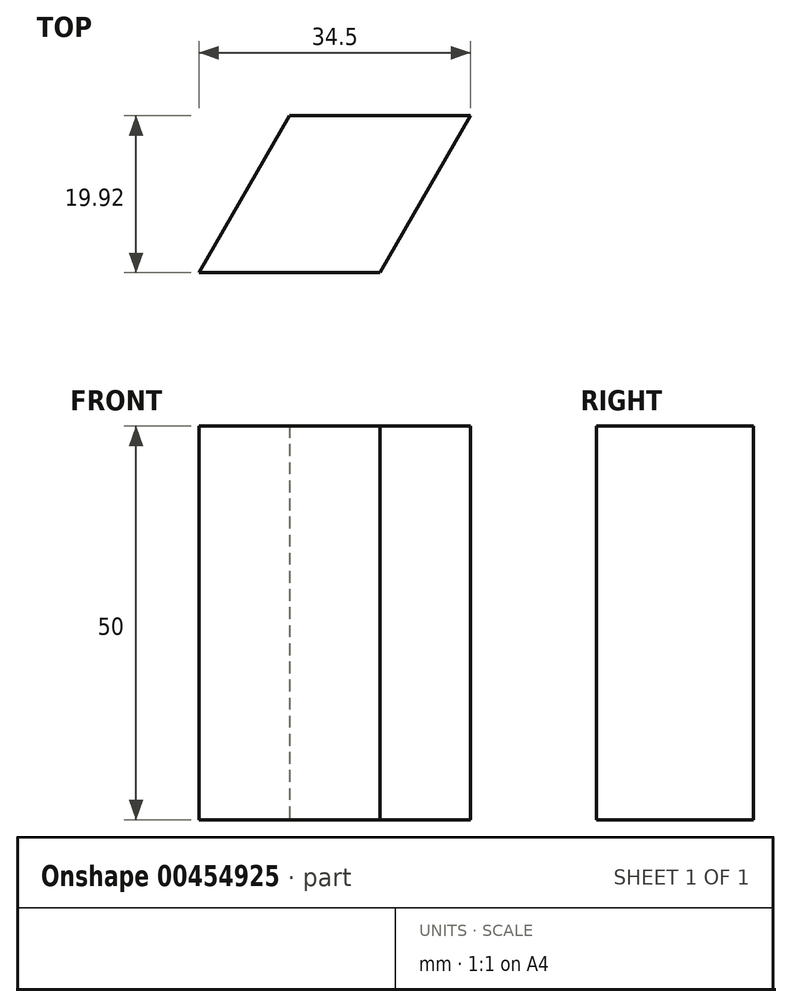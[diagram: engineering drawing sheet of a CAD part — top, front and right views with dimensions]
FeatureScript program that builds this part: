
annotation { "Feature Type Name" : "Feature", "Feature Type Description" : "" }
export const myFeature = defineFeature(function(context is Context, id is Id, definition is map)
    precondition{}
    {
        {
            var Q0;
            Q0=qCreatedBy(makeId("Top.planeOp"),FACE);
            var sketch = newSketch(context, id + "F0", { "sketchPlane" : qUnion([Q0])});
            skLineSegment(sketch, "E0", {"start": v(-11.5, -9.73) * mm, "end": v(11.5, -9.73) * mm});
            skLineSegment(sketch, "E1", {"start": v(11.5, -9.73) * mm, "end": v(23, 10.19) * mm});
            skLineSegment(sketch, "E2", {"start": v(23, 10.19) * mm, "end": v(0, 10.19) * mm});
            skLineSegment(sketch, "E3", {"start": v(0, 10.19) * mm, "end": v(-11.5, -9.73) * mm});
            skPoint(sketch, "E4", {"position": v(0, 0) * mm});
            skSolve(sketch);
        }
        {
            var Q0;
            Q0=qSketchRegion(id+"F0",true);
            var sketch = newSketch(context, id + "F1", { "sketchPlane" : qUnion([Q0])});
            skSolve(sketch);
        }
        {
            var Q0;
            Q0=makeQuery(id+"F0.imprint","IMPRINT",FACE,{"disambiguationData":[TD([[makeQuery(id+"F0.imprint","IMPRINT",EDGE,{"derivedFrom":sQuery(id+"F0.wireOp",EDGE,"E0")}),1.0]])]});
            var Q1;
            Q1=sQuery(id+"F0.wireOp",EDGE,"E0");
            var Q2;
            Q2=sQuery(id+"F0.wireOp",EDGE,"E1");
            var Q3;
            Q3=sQuery(id+"F0.wireOp",EDGE,"E3");
            var Q4;
            Q4=sQuery(id+"F0.wireOp",EDGE,"E2");
            extrude(context, id + "F2", {"entities" : qUnion([Q0]), "surfaceEntities" : qUnion([Q1, Q2, Q3, Q4]), "depth" : 50 * mm});
        }
    });
